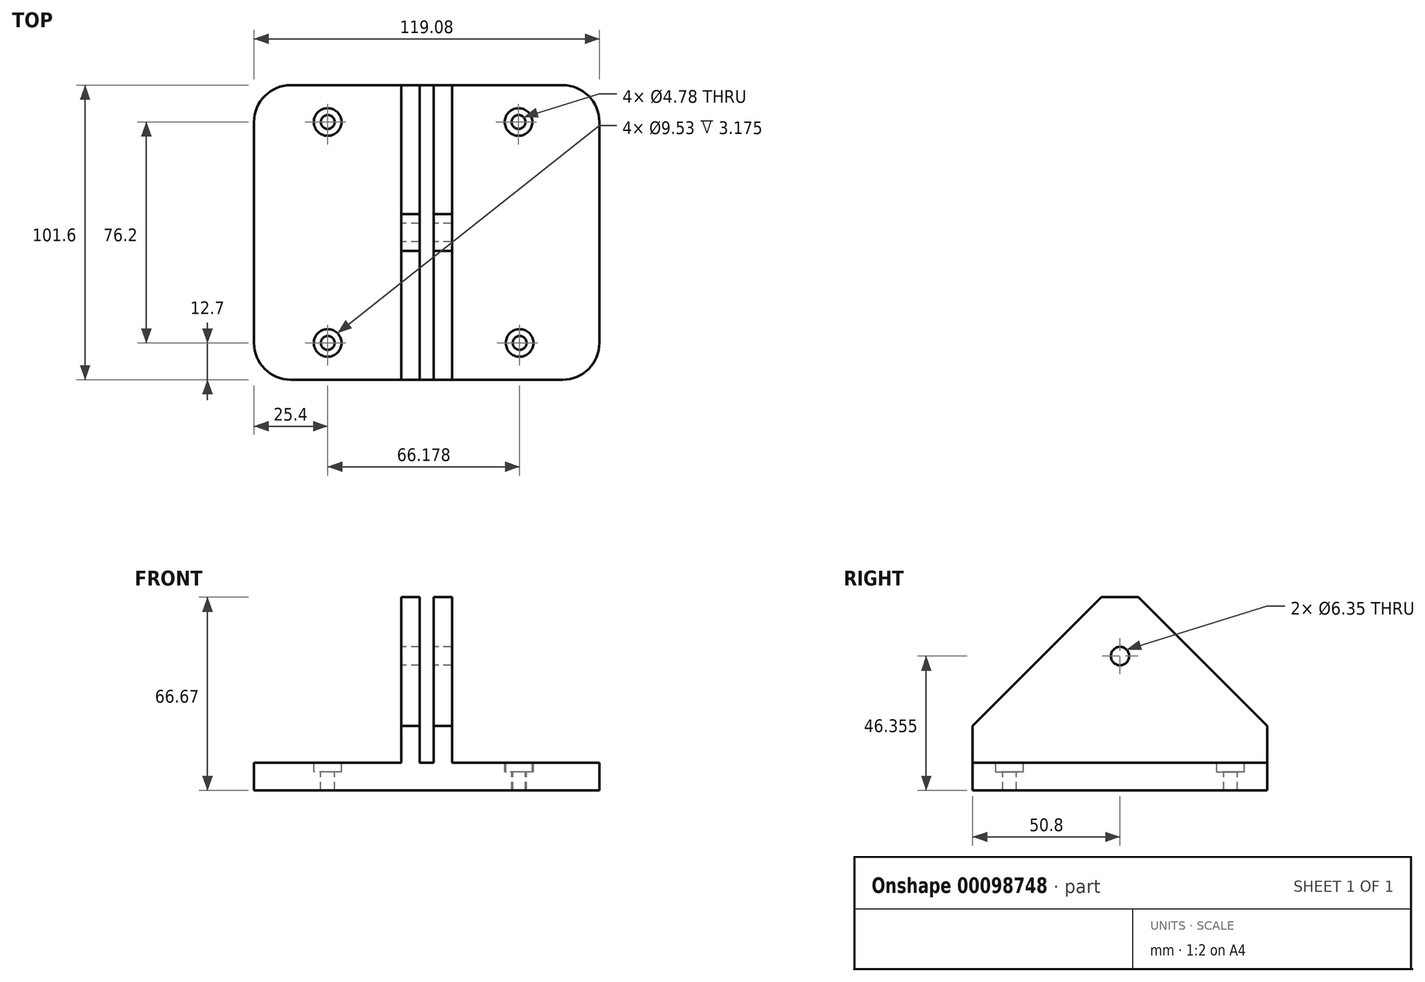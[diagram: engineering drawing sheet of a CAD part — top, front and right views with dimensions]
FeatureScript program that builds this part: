
annotation { "Feature Type Name" : "Feature", "Feature Type Description" : "" }
export const myFeature = defineFeature(function(context is Context, id is Id, definition is map)
    precondition{}
    {
        {
            var Q0;
            Q0=qCreatedBy(makeId("Front.planeOp"),FACE);
            var sketch = newSketch(context, id + "F0", { "sketchPlane" : qUnion([Q0])});
            skLineSegment(sketch, "E0", {"start": v(-57.15, 0) * mm, "end": v(61.93, 0) * mm});
            skLineSegment(sketch, "E1", {"start": v(61.93, 0) * mm, "end": v(61.93, 9.53) * mm});
            skLineSegment(sketch, "E2", {"start": v(61.93, 9.53) * mm, "end": v(11.13, 9.52) * mm});
            skLineSegment(sketch, "E3", {"start": v(11.13, 9.52) * mm, "end": v(11.13, 66.68) * mm});
            skLineSegment(sketch, "E4", {"start": v(11.13, 66.68) * mm, "end": v(4.78, 66.68) * mm});
            skLineSegment(sketch, "E5", {"start": v(4.78, 66.68) * mm, "end": v(4.78, 9.52) * mm});
            skLineSegment(sketch, "E6", {"start": v(4.78, 9.53) * mm, "end": v(0, 9.53) * mm});
            skLineSegment(sketch, "E7", {"start": v(0, 9.52) * mm, "end": v(0, 66.68) * mm});
            skLineSegment(sketch, "E8", {"start": v(0, 66.68) * mm, "end": v(-6.35, 66.68) * mm});
            skLineSegment(sketch, "E9", {"start": v(-6.35, 66.68) * mm, "end": v(-6.35, 9.52) * mm});
            skLineSegment(sketch, "E10", {"start": v(-6.35, 9.53) * mm, "end": v(-57.15, 9.53) * mm});
            skLineSegment(sketch, "E11", {"start": v(-57.15, 9.53) * mm, "end": v(-57.15, 0) * mm});
            skSolve(sketch);
        }
        {
            var Q0;
            Q0 = qSketchRegion(id + "F0", true);
            extrude(context, id + "F1", {"entities" : qUnion([Q0]), "depth" : 101.6 * mm});
        }
        {
            var Q0;
            Q0=makeQuery(id+"F1.opExtrude","SWEPT_FACE",FACE,{"disambiguationData":[OSD([sQuery(id+"F0.wireOp",EDGE,"E10")])]});
            var sketch = newSketch(context, id + "F2", { "sketchPlane" : qUnion([Q0])});
            skPoint(sketch, "E12", {"position": v(-31.75, -88.9) * mm});
            skPoint(sketch, "E12.positionSnap0", {"position": v(-31.75, -101.6) * mm});
            skPoint(sketch, "E13", {"position": v(-31.75, -12.7) * mm});
            skPoint(sketch, "E13.positionSnap0", {"position": v(-31.75, 0) * mm});
            skPoint(sketch, "E14", {"position": v(34.06, -12.7) * mm});
            skPoint(sketch, "E15", {"position": v(34.43, -88.9) * mm});
            skSolve(sketch);
        }
        {
            var Q0;
            Q0=sQuery(id+"F2.wireOp",VERTEX,"E15");
            var Q1;
            Q1=sQuery(id+"F2.wireOp",VERTEX,"E14");
            var Q2;
            Q2=sQuery(id+"F2.wireOp",VERTEX,"E13");
            var Q3;
            Q3=sQuery(id+"F2.wireOp",VERTEX,"E12");
            var Q4;
            Q4=makeQuery(id+"F1.opExtrude","SWEPT_BODY",BODY,{"disambiguationData":[OSD([sQuery(id+"F0.wireOp",EDGE,"E0"),sQuery(id+"F0.wireOp",EDGE,"E1"),sQuery(id+"F0.wireOp",EDGE,"E2"),sQuery(id+"F0.wireOp",EDGE,"E3"),sQuery(id+"F0.wireOp",EDGE,"E4"),sQuery(id+"F0.wireOp",EDGE,"E5"),sQuery(id+"F0.wireOp",EDGE,"E6"),sQuery(id+"F0.wireOp",EDGE,"E7"),sQuery(id+"F0.wireOp",EDGE,"E8"),sQuery(id+"F0.wireOp",EDGE,"E9"),sQuery(id+"F0.wireOp",EDGE,"E10"),sQuery(id+"F0.wireOp",EDGE,"E11")])]});
            hole(context, id + "F3", {"style" : HoleStyle.C_BORE, "endStyle" : HoleEndStyle.THROUGH, "holeDiameter" : 4.78 * mm, "cBoreDiameter" : 9.52 * mm, "cBoreDepth" : 3.17 * mm, "locations" : qUnion([Q0, Q1, Q2, Q3]), "scope" : qUnion([Q4]), "isTappedThrough" : true});
        }
        {
            var Q0;
            Q0=makeQuery(id+"F1.opExtrude","SWEPT_FACE",FACE,{"disambiguationData":[OSD([sQuery(id+"F0.wireOp",EDGE,"E9")])]});
            var sketch = newSketch(context, id + "F4", { "sketchPlane" : qUnion([Q0])});
            skPoint(sketch, "E16", {"position": v(50.8, 46.35) * mm});
            skPoint(sketch, "E16.positionSnap0", {"position": v(50.8, 9.53) * mm});
            skSolve(sketch);
        }
        {
            var Q0;
            Q0=sQuery(id+"F4.wireOp",VERTEX,"E16");
            var Q1;
            Q1=makeQuery(id+"F1.opExtrude","SWEPT_BODY",BODY,{"disambiguationData":[OSD([sQuery(id+"F0.wireOp",EDGE,"E0"),sQuery(id+"F0.wireOp",EDGE,"E1"),sQuery(id+"F0.wireOp",EDGE,"E2"),sQuery(id+"F0.wireOp",EDGE,"E3"),sQuery(id+"F0.wireOp",EDGE,"E4"),sQuery(id+"F0.wireOp",EDGE,"E5"),sQuery(id+"F0.wireOp",EDGE,"E6"),sQuery(id+"F0.wireOp",EDGE,"E7"),sQuery(id+"F0.wireOp",EDGE,"E8"),sQuery(id+"F0.wireOp",EDGE,"E9"),sQuery(id+"F0.wireOp",EDGE,"E10"),sQuery(id+"F0.wireOp",EDGE,"E11")])]});
            hole(context, id + "F5", {"style" : HoleStyle.SIMPLE, "endStyle" : HoleEndStyle.THROUGH, "holeDiameter" : 6.35 * mm, "locations" : qUnion([Q0]), "scope" : qUnion([Q1]), "isTappedThrough" : true});
        }
        {
            var Q0;
            Q0=makeQuery(id+"F1.opExtrude","CAP_EDGE",EDGE,{"disambiguationData":[OSD([sQuery(id+"F0.wireOp",EDGE,"E8")])],"isStart":false});
            var Q1;
            Q1=makeQuery(id+"F1.opExtrude","CAP_EDGE",EDGE,{"disambiguationData":[OSD([sQuery(id+"F0.wireOp",EDGE,"E4")])],"isStart":false});
            var Q2;
            Q2=makeQuery(id+"F1.opExtrude","CAP_EDGE",EDGE,{"disambiguationData":[OSD([sQuery(id+"F0.wireOp",EDGE,"E4")])],"isStart":true});
            var Q3;
            Q3=makeQuery(id+"F1.opExtrude","CAP_EDGE",EDGE,{"disambiguationData":[OSD([sQuery(id+"F0.wireOp",EDGE,"E8")])],"isStart":true});
            chamfer(context, id + "F6", {"entities" : qUnion([Q0, Q1, Q2, Q3]), "width" : 44.45 * mm, "tangentPropagation" : true});
        }
        {
            var Q0;
            Q0=makeQuery(id+"F1.opExtrude","CAP_EDGE",EDGE,{"disambiguationData":[OSD([sQuery(id+"F0.wireOp",EDGE,"E11")])],"isStart":false});
            var Q1;
            Q1=makeQuery(id+"F1.opExtrude","CAP_EDGE",EDGE,{"disambiguationData":[OSD([sQuery(id+"F0.wireOp",EDGE,"E11")])],"isStart":true});
            var Q2;
            Q2=makeQuery(id+"F1.opExtrude","CAP_EDGE",EDGE,{"disambiguationData":[OSD([sQuery(id+"F0.wireOp",EDGE,"E1")])],"isStart":false});
            var Q3;
            Q3=makeQuery(id+"F1.opExtrude","CAP_EDGE",EDGE,{"disambiguationData":[OSD([sQuery(id+"F0.wireOp",EDGE,"E1")])],"isStart":true});
            fillet(context, id + "F7", {"entities" : qUnion([Q0, Q1, Q2, Q3]), "radius" : 12.7 * mm, "tangentPropagation" : true, "allowEdgeOverflow" : false});
        }
    });
